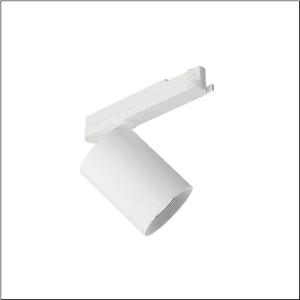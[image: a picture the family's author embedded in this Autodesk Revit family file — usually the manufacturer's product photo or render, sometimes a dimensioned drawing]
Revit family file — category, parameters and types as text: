
# Revit family: spot_21_51se12mba5b
name_source: partatom
category: Lighting Fixtures
units: mm (PartAtom-declared; Revit-internal decimal feet)

## family parameters
Cut with Voids When Loaded = No
Host = Face
Light Source = No
Part Type = Normal
Room Calculation Point = No
Round Connector Dimension = Use Diameter
Shared = No

## types (1)
- --- (1 x LED, 5240 lm, 41.7 W, 2700K)
    Apparent Load = 42 VA
    CIE Flux Codes = 95 98 99 100 100
    Color Rendering = 90
    Color Temperature = 2700K
    Default Elevation = 1800 mm
    Description = Spot 21, directional spotlight, light control with lens, of PMMA, LED rated luminous flux: 5.040lm, light colour: 927, control gear: ECG Multilumen, with 3-phase adapter, mains connection: 220..240V, AC, 50/60Hz, of aluminium, traffic white (RAL 9016), length: 213mm, diameter: 105mm, protection rating (complete): IP20, insulation class (complete): insulation class I (protective earthing), certification: CE, impact resistance: IK02, permissible ambient temperature for indoor applications: -20..+40°C, packaging unit: 1 piece
    Height = 175 mm
    Lamp = 1 x LED
    Lamp Light Flux = 5240 lm
    Lamp Power = 41.7 W
    Lamp count = 1
    Length = 105 mm
    Luminous efficacy = 126 lm/W
    Manufacturer = Siteco
    ModVariant = No
    Model = 51SE12MBA5B
    Mounting Place = Ceiling
    Mounting Type = Pendant
    Number of Poles = 1
    OnlyDefault = Yes
    Power Factor = 1
    Product Name = Spot 21
    Product group = directional spotlight
    ProductGroupID = 905
    Protection Class = Protection class I
    Protection Degree = IP 20
    RLX_Detail_Level = 1
    RLX_Emergency_Light_Flux = 0 lm
    RLX_Emergency_Type = 0
    RLX_Emergency_Type_DB = No
    RlxData = <blob elided: 17645 chars, md5=d0f3f7c1>
    Socket = socket
    Standby Power = 0 W
    System Light Flux = 5240 lm
    System Power = 42 W
    Type Comments = factory setting: luminous flux: 100 % | (ON | ON | ON | ON) | 1050 mA
    Type Image = l_1003976.jpg
    URL = http://relux.com
    VarID = @adj_076053
    Voltage = 0 V
    Weight = 0.00 kg
    Width = 0 mm  [stored 0 ft]

note: [stored X ft] marks values corroborated as IEEE doubles in the binary element streams (Revit-internal decimal feet)

## geometry (parser evidence)
native form markers: Blend x4, Sweep x10
no freeform markers — native parametric forms only
